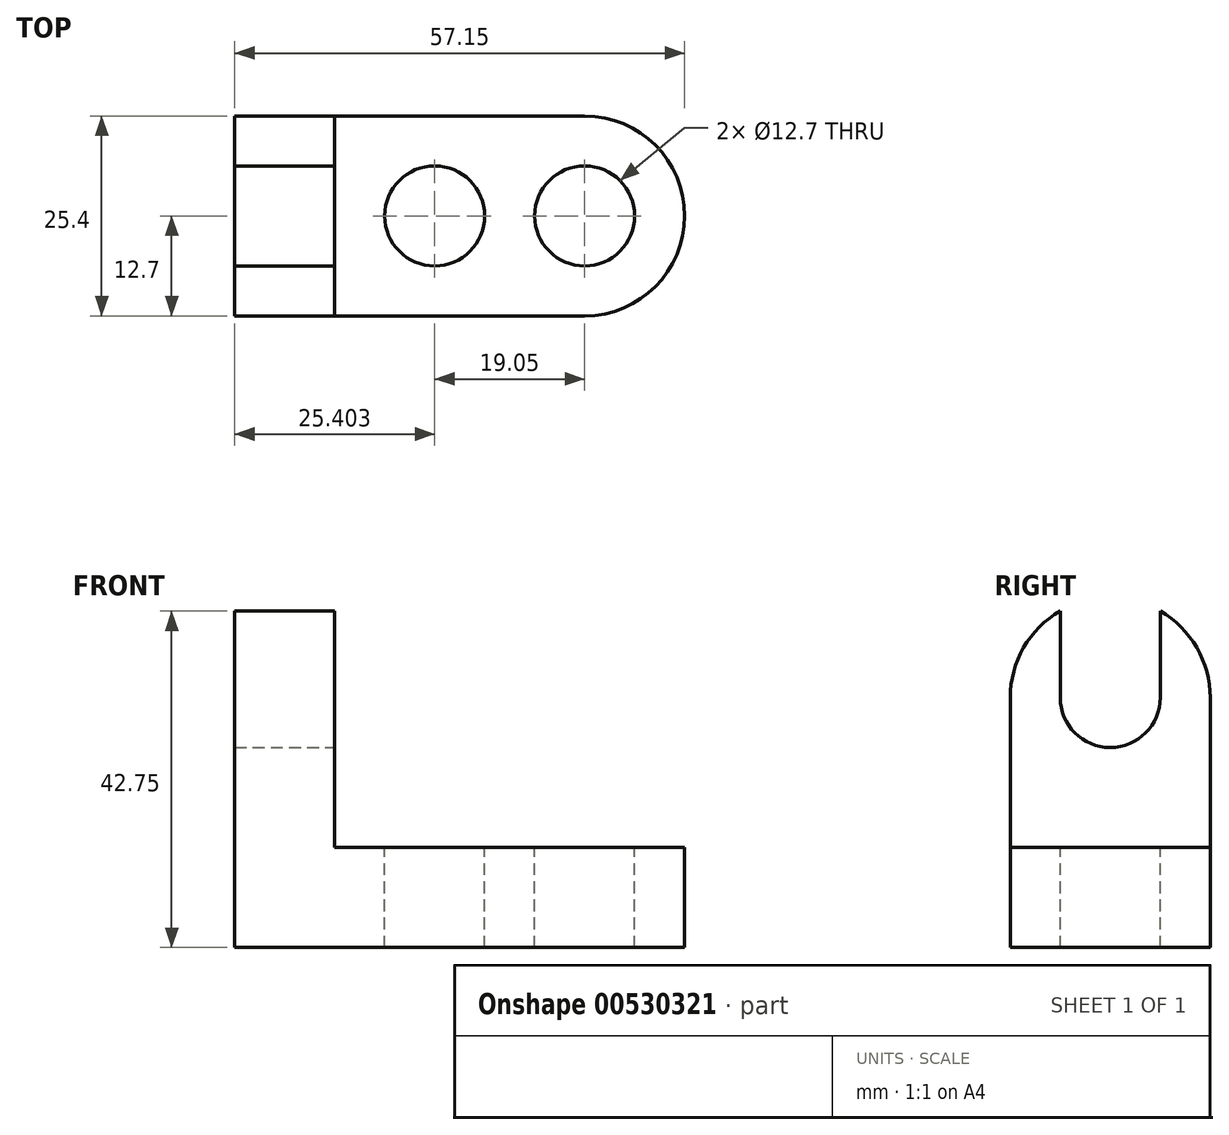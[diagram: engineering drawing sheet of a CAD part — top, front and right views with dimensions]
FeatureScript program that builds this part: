
annotation { "Feature Type Name" : "Feature", "Feature Type Description" : "" }
export const myFeature = defineFeature(function(context is Context, id is Id, definition is map)
    precondition{}
    {
        {
            var Q0;
            Q0=qCreatedBy(makeId("Front.planeOp"),FACE);
            var sketch = newSketch(context, id + "F0", { "sketchPlane" : qUnion([Q0])});
            skLineSegment(sketch, "E0", {"start": v(-69.99, 59.94) * mm, "end": v(-69.99, 15.5) * mm});
            skLineSegment(sketch, "E1", {"start": v(-69.99, 15.5) * mm, "end": v(-12.84, 15.5) * mm});
            skLineSegment(sketch, "E2", {"start": v(-12.84, 15.5) * mm, "end": v(-12.84, 28.2) * mm});
            skLineSegment(sketch, "E3", {"start": v(-12.84, 28.2) * mm, "end": v(-57.29, 28.2) * mm});
            skLineSegment(sketch, "E4", {"start": v(-69.99, 59.94) * mm, "end": v(-57.29, 59.94) * mm});
            skLineSegment(sketch, "E5", {"start": v(-57.29, 59.94) * mm, "end": v(-57.29, 28.2) * mm});
            skSolve(sketch);
        }
        {
            var Q0;
            Q0=makeQuery(id+"F0.imprint","IMPRINT",FACE,{"disambiguationData":[TD([[makeQuery(id+"F0.imprint","IMPRINT",EDGE,{"derivedFrom":sQuery(id+"F0.wireOp",EDGE,"E0")}),1.0]])]});
            extrude(context, id + "F1", {"entities" : qUnion([Q0]), "depth" : 25.4 * mm, "offsetDistance" : 25.4 * mm});
        }
        {
            var Q0;
            Q0=makeQuery(id+"F1.opExtrude","SWEPT_FACE",FACE,{"disambiguationData":[OSD([sQuery(id+"F0.wireOp",EDGE,"E3")])]});
            var sketch = newSketch(context, id + "F2", { "sketchPlane" : qUnion([Q0])});
            skCircle(sketch, "E6", {"center": v(-25.54, -12.7) * mm, "radius": 6.35 * mm});
            skCircle(sketch, "E7", {"center": v(-44.59, -12.7) * mm, "radius": 6.35 * mm});
            skLineSegment(sketch, "E8", {"start": v(-25.54, -6.35) * mm, "end": v(-25.54, 0) * mm});
            skPoint(sketch, "E8.endSnap0", {"position": v(-35.06, 0) * mm});
            skLineSegment(sketch, "E9", {"start": v(-25.54, -19.05) * mm, "end": v(-25.54, -25.4) * mm});
            skArc(sketch, "E10", {"start": v(-25.54, -25.4) * mm, "mid": v(-12.84, -12.7) * mm, "end": v(-25.54, 0) * mm});
            skSolve(sketch);
        }
        {
            var Q0;
            {var subQ0=sQuery(id+"F2.wireOp",EDGE,"E10");var subQ1=sQuery(id+"F0.wireOp",EDGE,"E3");var subQ2=makeQuery(id+"F1.opExtrude","CAP_EDGE",EDGE,{"disambiguationData":[OSD([subQ1])],"isStart":false});var subQ3=makeQuery(id+"F2.imprint","INTERSECT",VERTEX,{"derivedFrom":[subQ2,sQuery(id+"F2.wireOp",EDGE,"E9"),subQ0]});Q0=makeQuery(id+"F2.imprint","IMPRINT",FACE,{"disambiguationData":[TD([[makeQuery(id+"F2.imprint","IMPRINT",EDGE,{"disambiguationData":[TD([[subQ3,-1.0]])],"derivedFrom":subQ0}),-1.0]])]});}
            var Q1;
            {var subQ0=sQuery(id+"F2.wireOp",EDGE,"E10");var subQ1=sQuery(id+"F0.wireOp",EDGE,"E3");var subQ2=makeQuery(id+"F1.opExtrude","CAP_EDGE",EDGE,{"disambiguationData":[OSD([subQ1])],"isStart":true});var subQ3=makeQuery(id+"F2.imprint","INTERSECT",VERTEX,{"derivedFrom":[subQ2,sQuery(id+"F2.wireOp",EDGE,"E8"),subQ0]});Q1=makeQuery(id+"F2.imprint","IMPRINT",FACE,{"disambiguationData":[TD([[makeQuery(id+"F2.imprint","IMPRINT",EDGE,{"disambiguationData":[TD([[subQ3,1.0]])],"derivedFrom":subQ0}),-1.0]])]});}
            var Q2;
            {var subQ0=sQuery(id+"F2.wireOp",EDGE,"E6");var subQ1=makeQuery(id+"F2.imprint","INTERSECT",VERTEX,{"derivedFrom":[subQ0,sQuery(id+"F2.wireOp",EDGE,"E8")]});Q2=makeQuery(id+"F2.imprint","IMPRINT",FACE,{"disambiguationData":[TD([[makeQuery(id+"F2.imprint","IMPRINT",EDGE,{"disambiguationData":[TD([[subQ1,-1.0]])],"derivedFrom":subQ0}),1.0]])]});}
            var Q3;
            Q3=makeQuery(id+"F2.imprint","IMPRINT",FACE,{"disambiguationData":[TD([[makeQuery(id+"F2.imprint","IMPRINT",EDGE,{"derivedFrom":sQuery(id+"F2.wireOp",EDGE,"E7")}),1.0]])]});
            extrude(context, id + "F3", {"entities" : qUnion([Q0, Q1, Q2, Q3]), "operationType" : NewBodyOperationType.REMOVE, "endBound" : BoundingType.THROUGH_ALL, "oppositeDirection" : true, "depth" : 25.4 * mm, "offsetDistance" : 25.4 * mm});
        }
        {
            var Q0;
            Q0=makeQuery(id+"F1.opExtrude","SWEPT_FACE",FACE,{"disambiguationData":[OSD([sQuery(id+"F0.wireOp",EDGE,"E5")])]});
            var sketch = newSketch(context, id + "F4", { "sketchPlane" : qUnion([Q0])});
            skCircle(sketch, "E11", {"center": v(-12.7, 47.24) * mm, "radius": 6.35 * mm});
            skLineSegment(sketch, "E12", {"start": v(-12.7, 47.24) * mm, "end": v(-25.4, 47.24) * mm});
            skLineSegment(sketch, "E13", {"start": v(-12.7, 47.24) * mm, "end": v(0, 47.24) * mm});
            skArc(sketch, "E14", {"start": v(0, 47.24) * mm, "mid": v(-12.7, 59.94) * mm, "end": v(-25.4, 47.24) * mm});
            skLineSegment(sketch, "E15", {"start": v(-19.05, 47.24) * mm, "end": v(-19.05, 59.94) * mm});
            skLineSegment(sketch, "E16", {"start": v(-6.35, 47.24) * mm, "end": v(-6.35, 59.94) * mm});
            skSolve(sketch);
        }
        {
            var Q0;
            {var subQ0=sQuery(id+"F4.wireOp",EDGE,"E14");var subQ4=sQuery(id+"F4.wireOp",EDGE,"E15");var subQ5=makeQuery(id+"F4.imprint","INTERSECT",VERTEX,{"derivedFrom":[subQ0,subQ4]});Q0=makeQuery(id+"F4.imprint","IMPRINT",FACE,{"disambiguationData":[TD([[makeQuery(id+"F4.imprint","IMPRINT",EDGE,{"disambiguationData":[TD([[subQ5,-1.0]])],"derivedFrom":subQ0}),-1.0]])]});}
            var Q1;
            {var subQ0=sQuery(id+"F4.wireOp",EDGE,"E14");var subQ4=sQuery(id+"F4.wireOp",EDGE,"E16");var subQ5=makeQuery(id+"F4.imprint","INTERSECT",VERTEX,{"derivedFrom":[subQ0,subQ4]});Q1=makeQuery(id+"F4.imprint","IMPRINT",FACE,{"disambiguationData":[TD([[makeQuery(id+"F4.imprint","IMPRINT",EDGE,{"disambiguationData":[TD([[subQ5,1.0]])],"derivedFrom":subQ0}),-1.0]])]});}
            var Q2;
            {var subQ0=sQuery(id+"F4.wireOp",EDGE,"E16");var subQ1=sQuery(id+"F4.wireOp",EDGE,"E14");var subQ2=makeQuery(id+"F4.imprint","INTERSECT",VERTEX,{"derivedFrom":[subQ1,subQ0]});Q2=makeQuery(id+"F4.imprint","IMPRINT",FACE,{"disambiguationData":[TD([[makeQuery(id+"F4.imprint","IMPRINT",EDGE,{"disambiguationData":[TD([[subQ2,-1.0]])],"derivedFrom":subQ1}),-1.0]])]});}
            var Q3;
            {var subQ0=sQuery(id+"F4.wireOp",EDGE,"E15");var subQ1=sQuery(id+"F4.wireOp",EDGE,"E14");var subQ2=makeQuery(id+"F4.imprint","INTERSECT",VERTEX,{"derivedFrom":[subQ1,subQ0]});Q3=makeQuery(id+"F4.imprint","IMPRINT",FACE,{"disambiguationData":[TD([[makeQuery(id+"F4.imprint","IMPRINT",EDGE,{"disambiguationData":[TD([[subQ2,1.0]])],"derivedFrom":subQ1}),-1.0]])]});}
            var Q4;
            {var subQ0=sQuery(id+"F4.wireOp",EDGE,"E12");var subQ3=sQuery(id+"F4.wireOp",EDGE,"E13");var subQ5=makeQuery(id+"F4.imprint","INTERSECT",VERTEX,{"derivedFrom":[subQ0,subQ3]});Q4=makeQuery(id+"F4.imprint","IMPRINT",FACE,{"disambiguationData":[TD([[makeQuery(id+"F4.imprint","IMPRINT",EDGE,{"disambiguationData":[TD([[subQ5,-1.0]])],"derivedFrom":subQ0}),-1.0]])]});}
            var Q5;
            {var subQ0=sQuery(id+"F4.wireOp",EDGE,"E12");var subQ3=sQuery(id+"F4.wireOp",EDGE,"E13");var subQ5=makeQuery(id+"F4.imprint","INTERSECT",VERTEX,{"derivedFrom":[subQ0,subQ3]});Q5=makeQuery(id+"F4.imprint","IMPRINT",FACE,{"disambiguationData":[TD([[makeQuery(id+"F4.imprint","IMPRINT",EDGE,{"disambiguationData":[TD([[subQ5,-1.0]])],"derivedFrom":subQ0}),1.0]])]});}
            var Q6;
            {var subQ1=sQuery(id+"F4.wireOp",EDGE,"E14");var subQ4=sQuery(id+"F4.wireOp",EDGE,"E16");var subQ5=makeQuery(id+"F4.imprint","INTERSECT",VERTEX,{"derivedFrom":[subQ1,subQ4]});Q6=makeQuery(id+"F4.imprint","IMPRINT",FACE,{"disambiguationData":[TD([[makeQuery(id+"F4.imprint","IMPRINT",EDGE,{"disambiguationData":[TD([[subQ5,-1.0]])],"derivedFrom":subQ1}),1.0]])]});}
            extrude(context, id + "F5", {"entities" : qUnion([Q0, Q1, Q2, Q3, Q4, Q5, Q6]), "operationType" : NewBodyOperationType.REMOVE, "endBound" : BoundingType.THROUGH_ALL, "oppositeDirection" : true, "depth" : 25.4 * mm, "offsetDistance" : 25.4 * mm});
        }
    });
